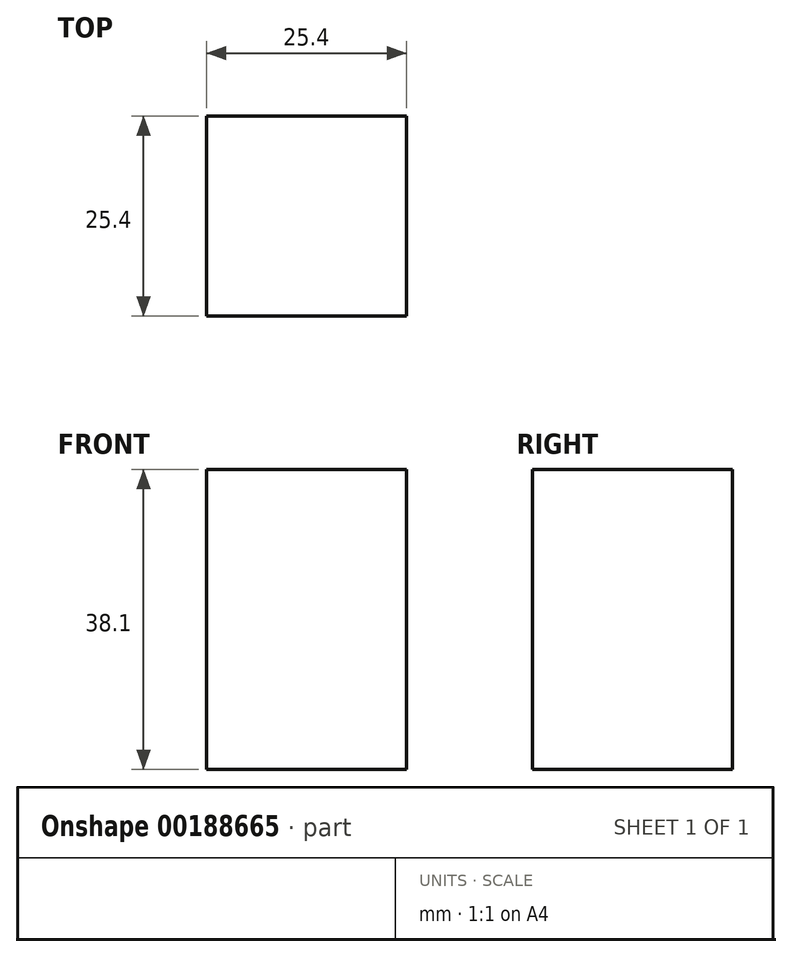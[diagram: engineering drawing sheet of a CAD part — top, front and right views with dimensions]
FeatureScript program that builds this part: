
annotation { "Feature Type Name" : "Feature", "Feature Type Description" : "" }
export const myFeature = defineFeature(function(context is Context, id is Id, definition is map)
    precondition{}
    {
        {
            var Q0;
            Q0=qCreatedBy(makeId("Front.planeOp"),FACE);
            var sketch = newSketch(context, id + "F0", { "sketchPlane" : qUnion([Q0])});
            skLineSegment(sketch, "E0.bottom", {"start": v(-12.7, 19.05) * mm, "end": v(12.7, 19.05) * mm});
            skLineSegment(sketch, "E0.top", {"start": v(-12.7, -19.05) * mm, "end": v(12.7, -19.05) * mm});
            skLineSegment(sketch, "E0.left", {"start": v(-12.7, 19.05) * mm, "end": v(-12.7, -19.05) * mm});
            skLineSegment(sketch, "E0.right", {"start": v(12.7, 19.05) * mm, "end": v(12.7, -19.05) * mm});
            skSolve(sketch);
        }
        {
            var Q0;
            Q0=makeQuery(id+"F0.imprint","IMPRINT",FACE,{"disambiguationData":[TD([[makeQuery(id+"F0.imprint","IMPRINT",EDGE,{"derivedFrom":sQuery(id+"F0.wireOp",EDGE,"E0.bottom")}),-1.0]])]});
            extrude(context, id + "F1", {"entities" : qUnion([Q0]), "depth" : 25.4 * mm});
        }
    });
